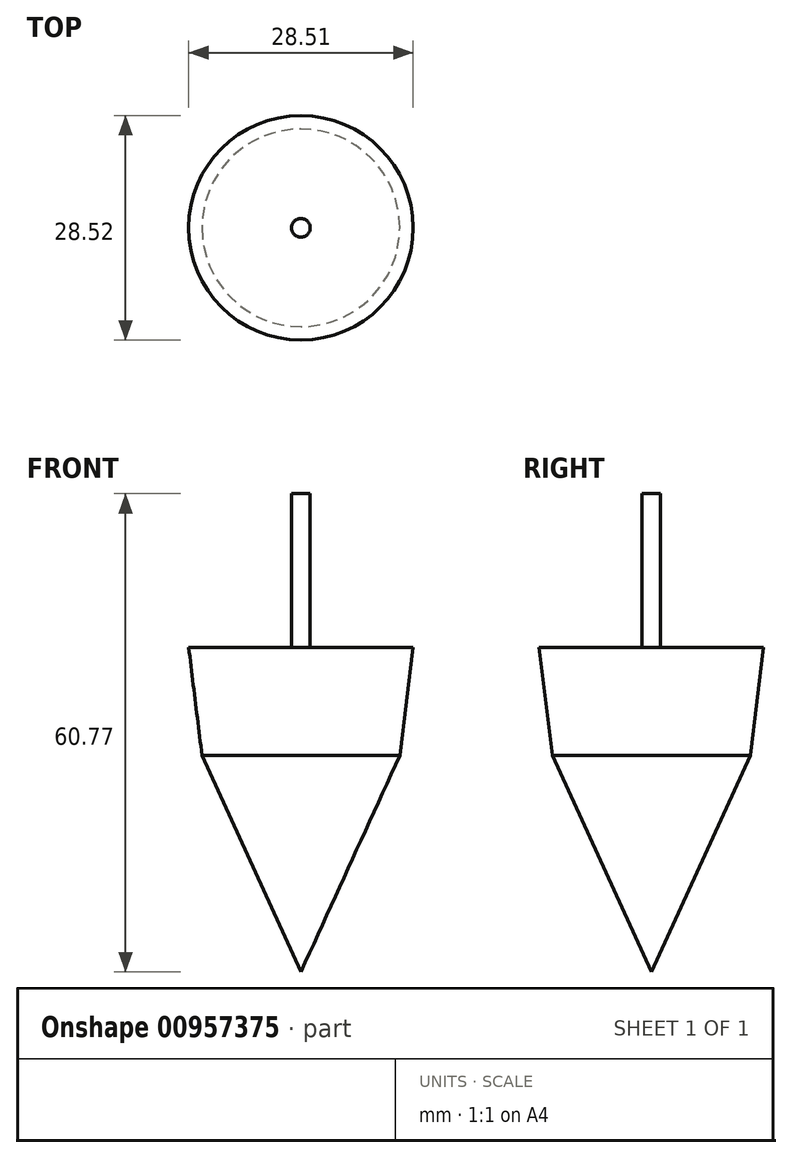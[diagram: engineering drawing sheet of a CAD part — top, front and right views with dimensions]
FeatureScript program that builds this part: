
annotation { "Feature Type Name" : "Feature", "Feature Type Description" : "" }
export const myFeature = defineFeature(function(context is Context, id is Id, definition is map)
    precondition{}
    {
        {
            var Q0;
            Q0=qCreatedBy(makeId("Front.planeOp"),FACE);
            var sketch = newSketch(context, id + "F0", { "sketchPlane" : qUnion([Q0])});
            skLineSegment(sketch, "E0", {"start": v(22.75, 8.45) * mm, "end": v(10.19, -19.05) * mm});
            skLineSegment(sketch, "E1", {"start": v(10.19, -19.05) * mm, "end": v(10.19, 22.2) * mm});
            skLineSegment(sketch, "E2", {"start": v(10.19, 22.2) * mm, "end": v(24.44, 22.2) * mm});
            skLineSegment(sketch, "E3", {"start": v(24.44, 22.2) * mm, "end": v(22.75, 8.45) * mm});
            skLineSegment(sketch, "E4", {"start": v(11.37, 22.2) * mm, "end": v(11.37, 41.72) * mm});
            skLineSegment(sketch, "E5", {"start": v(11.37, 41.72) * mm, "end": v(10.19, 41.72) * mm});
            skLineSegment(sketch, "E6", {"start": v(10.19, 41.72) * mm, "end": v(10.19, 22.2) * mm});
            skSolve(sketch);
        }
        {
            var Q0;
            Q0 = qSketchRegion(id + "F0", true);
            var Q1;
            Q1=sQuery(id+"F0.wireOp",EDGE,"E1");
            revolve(context, id + "F1", {"surfaceOperationType" : NewSurfaceOperationType.NEW, "entities" : qUnion([Q0]), "axis" : qUnion([Q1]), "revolveType" : RevolveType.FULL});
        }
    });
